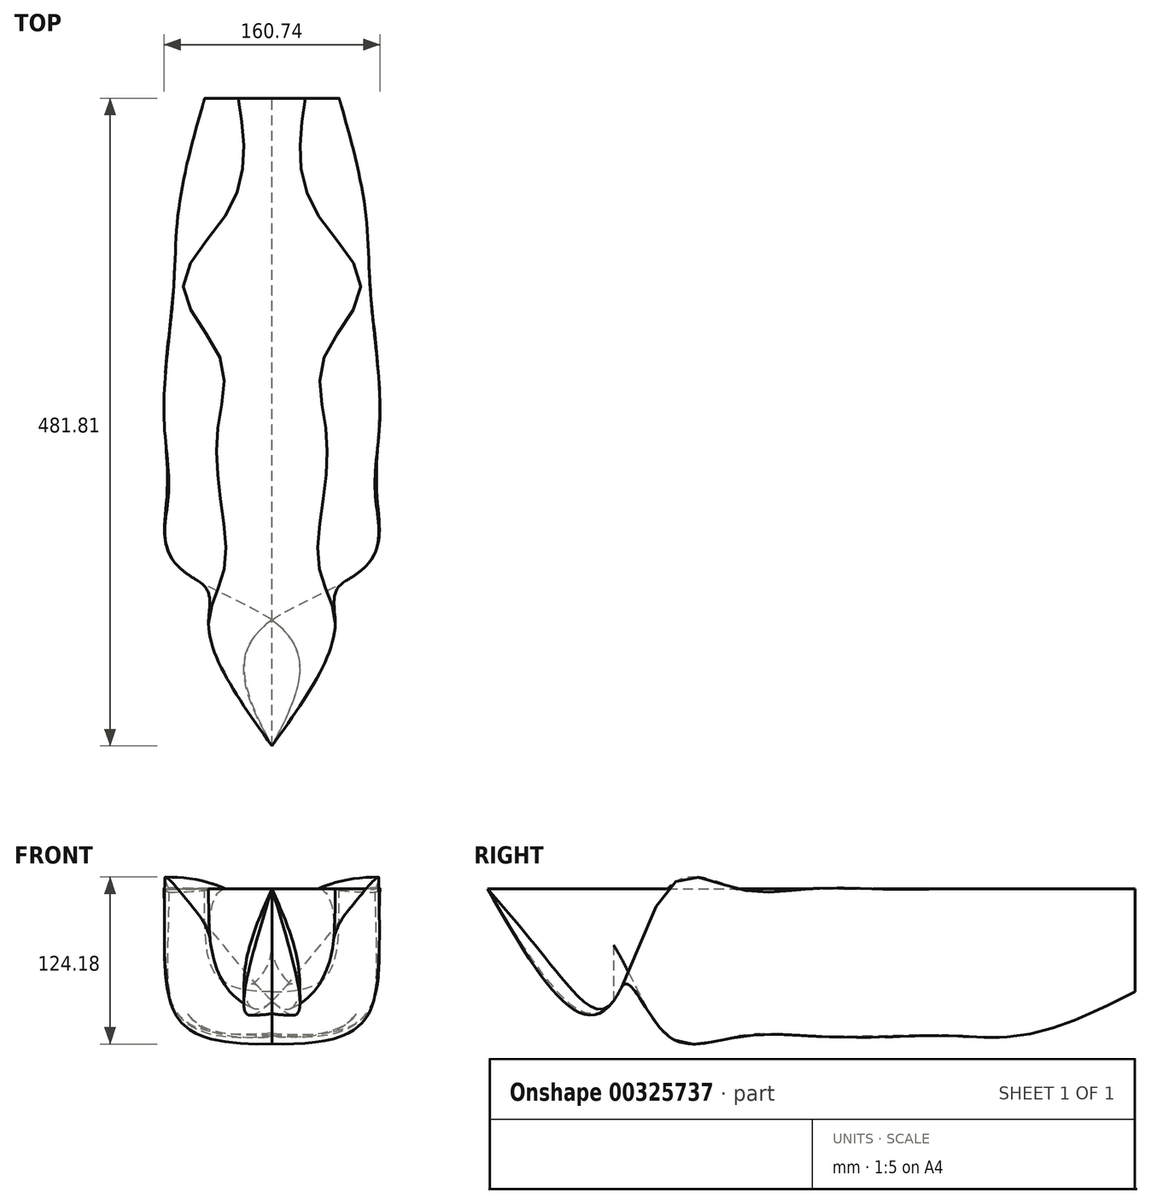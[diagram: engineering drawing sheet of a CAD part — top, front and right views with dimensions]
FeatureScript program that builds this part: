
annotation { "Feature Type Name" : "Feature", "Feature Type Description" : "" }
export const myFeature = defineFeature(function(context is Context, id is Id, definition is map)
    precondition{}
    {
        {
            var Q0;
            Q0=qCreatedBy(makeId("Front.planeOp"),FACE);
            var sketch = newSketch(context, id + "F0", { "sketchPlane" : qUnion([Q0])});
            skLineSegment(sketch, "E0", {"start": v(0, 0) * mm, "end": v(50, 0) * mm, "construction": true});
            skPoint(sketch, "E1", {"position": v(50, 0) * mm});
            skPoint(sketch, "E2", {"position": v(0, -76.5) * mm});
            skLineSegment(sketch, "E3", {"start": v(0, -76.5) * mm, "end": v(0, 0) * mm, "construction": true});
            skFitSpline(sketch, "E4", {"points": [v(0, -76.5) * mm, v(50, 0) * mm], "startDerivative": vector(150.57, -0.1) * mm, "endDerivative": vector(-0.6, 172.64) * mm});
            skLineSegment(sketch, "E5", {"start": v(0, 0) * mm, "end": v(50, 0) * mm});
            skLineSegment(sketch, "E6", {"start": v(0, 0) * mm, "end": v(0, -76.5) * mm});
            skSolve(sketch);
        }
        {
            var Q0;
            Q0=qCreatedBy(makeId("Front.planeOp"),FACE);
            cPlane(context, id + "F1", {"entities" : qUnion([Q0]), "cplaneType" : CPlaneType.OFFSET, "offset" : 87.89 * mm, "width" : 150 * mm, "height" : 150 * mm});
        }
        {
            var Q0;
            Q0=qCreatedBy(id+"F1.planeOp",FACE);
            var sketch = newSketch(context, id + "F2", { "sketchPlane" : qUnion([Q0])});
            skLineSegment(sketch, "E7", {"start": v(0, 0) * mm, "end": v(70, 0) * mm, "construction": true});
            skPoint(sketch, "E8", {"position": v(0, -109) * mm});
            skFitSpline(sketch, "E9", {"points": [v(0, -109) * mm, v(70, 0) * mm], "startDerivative": vector(234.89, -12.63) * mm, "endDerivative": vector(3.7, 249.63) * mm});
            skLineSegment(sketch, "E10", {"start": v(0, -109) * mm, "end": v(0, 0) * mm, "construction": true});
            skLineSegment(sketch, "E11", {"start": v(0, 0) * mm, "end": v(0, -109) * mm});
            skLineSegment(sketch, "E12", {"start": v(0, 0) * mm, "end": v(70, 0) * mm});
            skSolve(sketch);
        }
        {
            var Q0;
            Q0=qCreatedBy(id+"F1.planeOp",FACE);
            cPlane(context, id + "F3", {"entities" : qUnion([Q0]), "cplaneType" : CPlaneType.OFFSET, "offset" : 52 * mm, "width" : 150 * mm, "height" : 150 * mm});
        }
        {
            var Q0;
            Q0=qCreatedBy(id+"F3.planeOp",FACE);
            var sketch = newSketch(context, id + "F4", { "sketchPlane" : qUnion([Q0])});
            skLineSegment(sketch, "E13", {"start": v(0, 0) * mm, "end": v(66, 0) * mm, "construction": true});
            skPoint(sketch, "E14", {"position": v(0, -109) * mm});
            skLineSegment(sketch, "E15", {"start": v(0, -109) * mm, "end": v(0, 0) * mm, "construction": true});
            skFitSpline(sketch, "E16.MirrorCS", {"points": [v(73, 0) * mm, v(0, -109) * mm], "startDerivative": vector(0.66, -274.17) * mm, "endDerivative": vector(-226.93, 5.65) * mm});
            skLineSegment(sketch, "E17", {"start": v(0, 0) * mm, "end": v(66, 0) * mm});
            skLineSegment(sketch, "E18", {"start": v(0, 0) * mm, "end": v(0, -109) * mm});
            skLineSegment(sketch, "E19", {"start": v(0, 0) * mm, "end": v(73, 0) * mm});
            skSolve(sketch);
        }
        {
            var Q0;
            Q0=qCreatedBy(id+"F3.planeOp",FACE);
            cPlane(context, id + "F5", {"entities" : qUnion([Q0]), "cplaneType" : CPlaneType.OFFSET, "offset" : 52 * mm, "width" : 150 * mm, "height" : 150 * mm});
        }
        {
            var Q0;
            Q0=qCreatedBy(id+"F5.planeOp",FACE);
            var sketch = newSketch(context, id + "F6", { "sketchPlane" : qUnion([Q0])});
            skLineSegment(sketch, "E20", {"start": v(0, 0) * mm, "end": v(78, 0) * mm, "construction": true});
            skPoint(sketch, "E21", {"position": v(0, -109) * mm});
            skFitSpline(sketch, "E22", {"points": [v(0, -109) * mm, v(78, 0) * mm], "startDerivative": vector(269.3, -27.98) * mm, "endDerivative": vector(2.35, 224.48) * mm});
            skLineSegment(sketch, "E23", {"start": v(0, 0) * mm, "end": v(78, 0) * mm});
            skLineSegment(sketch, "E24", {"start": v(0, 0) * mm, "end": v(0, -109) * mm});
            skSolve(sketch);
        }
        {
            var Q0;
            Q0=qCreatedBy(id+"F5.planeOp",FACE);
            cPlane(context, id + "F7", {"entities" : qUnion([Q0]), "cplaneType" : CPlaneType.OFFSET, "offset" : 52 * mm, "width" : 150 * mm, "height" : 150 * mm});
        }
        {
            var Q0;
            Q0=qCreatedBy(id+"F7.planeOp",FACE);
            var sketch = newSketch(context, id + "F8", { "sketchPlane" : qUnion([Q0])});
            skLineSegment(sketch, "E25", {"start": v(0, 0) * mm, "end": v(80, 0) * mm, "construction": true});
            skPoint(sketch, "E26", {"position": v(0, -109) * mm});
            skFitSpline(sketch, "E27", {"points": [v(0, -109) * mm, v(80, 0) * mm], "startDerivative": vector(287.94, -11.65) * mm, "endDerivative": vector(10.45, 232) * mm});
            skLineSegment(sketch, "E28", {"start": v(0, -109) * mm, "end": v(0, 0) * mm});
            skLineSegment(sketch, "E29", {"start": v(80, 0) * mm, "end": v(0, 0) * mm});
            skSolve(sketch);
        }
        {
            var Q0;
            Q0=qCreatedBy(id+"F7.planeOp",FACE);
            cPlane(context, id + "F9", {"entities" : qUnion([Q0]), "cplaneType" : CPlaneType.OFFSET, "offset" : 52 * mm, "width" : 150 * mm, "height" : 150 * mm});
        }
        {
            var Q0;
            Q0=qCreatedBy(id+"F9.planeOp",FACE);
            var sketch = newSketch(context, id + "F10", { "sketchPlane" : qUnion([Q0])});
            skLineSegment(sketch, "E30", {"start": v(0, 0) * mm, "end": v(77, 0) * mm, "construction": true});
            skPoint(sketch, "E31", {"position": v(0, -109) * mm});
            skFitSpline(sketch, "E32", {"points": [v(0, -109) * mm, v(77, 0) * mm], "startDerivative": vector(264.56, -21.49) * mm, "endDerivative": vector(-4.95, 274.24) * mm});
            skLineSegment(sketch, "E33", {"start": v(0, -109) * mm, "end": v(0, 0) * mm});
            skLineSegment(sketch, "E34", {"start": v(77, 0) * mm, "end": v(0, 0) * mm});
            skSolve(sketch);
        }
        {
            var Q0;
            Q0=qCreatedBy(id+"F9.planeOp",FACE);
            cPlane(context, id + "F11", {"entities" : qUnion([Q0]), "cplaneType" : CPlaneType.OFFSET, "offset" : 52 * mm, "width" : 150 * mm, "height" : 150 * mm});
        }
        {
            var Q0;
            Q0=qCreatedBy(id+"F11.planeOp",FACE);
            var sketch = newSketch(context, id + "F12", { "sketchPlane" : qUnion([Q0])});
            skLineSegment(sketch, "E35", {"start": v(-70, 0) * mm, "end": v(0, 0) * mm, "construction": true});
            skLineSegment(sketch, "E36", {"start": v(0, 0) * mm, "end": v(70, 0) * mm, "construction": true});
            skPoint(sketch, "E37", {"position": v(0, -109) * mm});
            skFitSpline(sketch, "E38", {"points": [v(0, -109) * mm, v(70, 0) * mm], "startDerivative": vector(196.47, -0.23) * mm, "endDerivative": vector(-0.02, 268.03) * mm});
            skLineSegment(sketch, "E39", {"start": v(0, -109) * mm, "end": v(0, 0) * mm});
            skLineSegment(sketch, "E40", {"start": v(0, 0) * mm, "end": v(70, 0) * mm});
            skSolve(sketch);
        }
        {
            var Q0;
            Q0=qCreatedBy(id+"F11.planeOp",FACE);
            cPlane(context, id + "F13", {"entities" : qUnion([Q0]), "cplaneType" : CPlaneType.OFFSET, "offset" : 40.2 * mm, "width" : 150 * mm, "height" : 150 * mm});
        }
        {
            var Q0;
            Q0=qCreatedBy(id+"F13.planeOp",FACE);
            var sketch = newSketch(context, id + "F14", { "sketchPlane" : qUnion([Q0])});
            skLineSegment(sketch, "E41", {"start": v(-47, 0) * mm, "end": v(0, 0) * mm, "construction": true});
            skLineSegment(sketch, "E42", {"start": v(0, 0) * mm, "end": v(47, 0) * mm, "construction": true});
            skPoint(sketch, "E43", {"position": v(0, -83.35) * mm});
            skFitSpline(sketch, "E44", {"points": [v(0, -83.35) * mm, v(47, 0) * mm], "startDerivative": vector(126, -0.03) * mm, "endDerivative": vector(-1.76, 170.18) * mm});
            skLineSegment(sketch, "E45", {"start": v(0, -83.35) * mm, "end": v(0, 0) * mm});
            skLineSegment(sketch, "E46", {"start": v(0, 0) * mm, "end": v(47, 0) * mm});
            skSolve(sketch);
        }
        {
            var Q0;
            Q0=qCreatedBy(id+"F13.planeOp",FACE);
            cPlane(context, id + "F15", {"entities" : qUnion([Q0]), "cplaneType" : CPlaneType.OFFSET, "offset" : 93.72 * mm, "width" : 150 * mm, "height" : 150 * mm});
        }
        {
            var Q0;
            Q0=qCreatedBy(id+"F15.planeOp",FACE);
            var sketch = newSketch(context, id + "F16", { "sketchPlane" : qUnion([Q0])});
            skPoint(sketch, "E47", {"position": v(0, 0) * mm});
            skSolve(sketch);
        }
        {
            var Q0;
            Q0=sQuery(id+"F16.wireOp",VERTEX,"E47");
            var Q1;
            Q1=makeQuery(id+"F14.imprint","IMPRINT",FACE,{"disambiguationData":[TD([[makeQuery(id+"F14.imprint","IMPRINT",EDGE,{"derivedFrom":sQuery(id+"F14.wireOp",EDGE,"E44")}),1.0]])]});
            var Q2;
            Q2=makeQuery(id+"F12.imprint","IMPRINT",FACE,{"disambiguationData":[TD([[makeQuery(id+"F12.imprint","IMPRINT",EDGE,{"derivedFrom":sQuery(id+"F12.wireOp",EDGE,"E38")}),1.0]])]});
            var Q3;
            Q3=makeQuery(id+"F10.imprint","IMPRINT",FACE,{"disambiguationData":[TD([[makeQuery(id+"F10.imprint","IMPRINT",EDGE,{"derivedFrom":sQuery(id+"F10.wireOp",EDGE,"E32")}),1.0]])]});
            var Q4;
            Q4=makeQuery(id+"F8.imprint","IMPRINT",FACE,{"disambiguationData":[TD([[makeQuery(id+"F8.imprint","IMPRINT",EDGE,{"derivedFrom":sQuery(id+"F8.wireOp",EDGE,"E27")}),1.0]])]});
            var Q5;
            Q5=makeQuery(id+"F6.imprint","IMPRINT",FACE,{"disambiguationData":[TD([[makeQuery(id+"F6.imprint","IMPRINT",EDGE,{"derivedFrom":sQuery(id+"F6.wireOp",EDGE,"E22")}),1.0]])]});
            var Q6;
            {var subQ0=sQuery(id+"F4.wireOp",EDGE,"E16.MirrorCS");Q6=makeQuery(id+"F4.imprint","IMPRINT",FACE,{"disambiguationData":[TD([[makeQuery(id+"F4.imprint","IMPRINT",EDGE,{"derivedFrom":subQ0}),-1.0]])]});}
            var Q7;
            Q7=makeQuery(id+"F2.imprint","IMPRINT",FACE,{"disambiguationData":[TD([[makeQuery(id+"F2.imprint","IMPRINT",EDGE,{"derivedFrom":sQuery(id+"F2.wireOp",EDGE,"E9")}),1.0]])]});
            var Q8;
            Q8=makeQuery(id+"F0.imprint","IMPRINT",FACE,{"disambiguationData":[TD([[makeQuery(id+"F0.imprint","IMPRINT",EDGE,{"derivedFrom":sQuery(id+"F0.wireOp",EDGE,"E4")}),1.0]])]});
            loft(context, id + "F17", {"sheetProfilesArray" : [{ "sheetProfileEntities" : qUnion([Q0]) }, { "sheetProfileEntities" : qUnion([Q1]) }, { "sheetProfileEntities" : qUnion([Q2]) }, { "sheetProfileEntities" : qUnion([Q3]) }, { "sheetProfileEntities" : qUnion([Q4]) }, { "sheetProfileEntities" : qUnion([Q5]) }, { "sheetProfileEntities" : qUnion([Q6]) }, { "sheetProfileEntities" : qUnion([Q7]) }, { "sheetProfileEntities" : qUnion([Q8]) }]});
        }
        {
            var Q0;
            Q0=makeQuery(id+"F17.opLoft","SWEPT_BODY",BODY,{"disambiguationData":[OSD([makeQuery(id+"F0.imprint","IMPRINT",FACE,{"disambiguationData":[TD([[makeQuery(id+"F0.imprint","IMPRINT",EDGE,{"derivedFrom":sQuery(id+"F0.wireOp",EDGE,"E4")}),1.0]])]}),sQuery(id+"F2.wireOp",EDGE,"E11"),sQuery(id+"F4.wireOp",EDGE,"E19"),sQuery(id+"F6.wireOp",EDGE,"E24"),sQuery(id+"F8.wireOp",EDGE,"E27"),sQuery(id+"F10.wireOp",EDGE,"E32"),sQuery(id+"F12.wireOp",EDGE,"E39"),sQuery(id+"F14.wireOp",EDGE,"E45"),sQuery(id+"F16.wireOp",VERTEX,"E47")])]});
            var Q1;
            Q1=qCreatedBy(makeId("Right.planeOp"),FACE);
            mirror(context, id + "F18", {"operationType" : NewBodyOperationType.ADD, "entities" : qUnion([Q0]), "mirrorPlane" : qUnion([Q1])});
        }
    });
